# Revit family: Gira_213326
name_source: partatom
category: Elektroinstallationen
revit_build: Autodesk Revit 2017 (Build: 20160225_1515(x64)
units: mm (PartAtom-declared; Revit-internal decimal feet)

## family parameters
Basisbauteil = Fläche
Beim Laden mit Abzugskörper schneiden = Nein
Bemaßung runder Anschluss = Durchmesser verwenden
Beschriftungsausrichtung beibehalten = Nein
Gemeinsam genutzt = Nein
Raumberechnungspunkt = Nein
Teiletyp = Normal

## types (1)
- Gira_213326
    Andere Bussysteme = ohne
    Anzahl der Kanäle = 3
    Ausführung = Wandsender komplett
    Ausführung der Oberfläche = nicht zutreffend
    BIM = https://media.stage.bim.site und Tasten.rfa
    Bauelement = Sys55_Abdeckung_Schalten und Tasten
    Beschreibung = Wippenset 3fach mit Beschriftungsfeld System 55 Klar   Farbe Alu Hinweise : - Beschreibbare Wippensets und Wippensets mit Beschriftungsfeld können mit einer individuellen Beschriftung versehen werden. Die Bestellung wird über den Großhandel abgewickelt, der beim Bestellvorgang der Wippen angegeben wurde. - Beschreibbare Wippensets und Wippensets ohne Beschriftungsfeld sind aus Metall. Dies kann bei Funkanwendungen zu Reichweiteneinbußen führen. - Professionelle Beschriftung über den Gira Beschriftungsservice www.beschriftung.gira.de.
    Bussystem Funkbus = Nein
    Bussystem KNX = Ja
    Bussystem KNX-Funk = Nein
    Bussystem LON = Nein
    Bussystem Powernet = Nein
    Datenblatt = https://katalog.gira.de
    Farbe = Aluminium
    GTIN = 4010337081364
    HAN = 213326
    Hersteller = Gira
    Mit Busankopplung = Nein
    Montageart = Aufputz
    Oberfläche = sonstige
    Produktseite = http://katalog.gira.de
    RAL-Nummer (ähnlich) = 9010
    Transparent = Nein
    Typname = Wippenset 3f BSF System 55 Klar/F Alu
    URL = https://www.gira.de
    Vorgabe-Ansicht = 1219 mm
    Werkstoff = sonstige
    Werkstoffgüte = sonstige

## geometry (parser evidence)
native form markers: Sweep x7
no freeform markers — native parametric forms only
